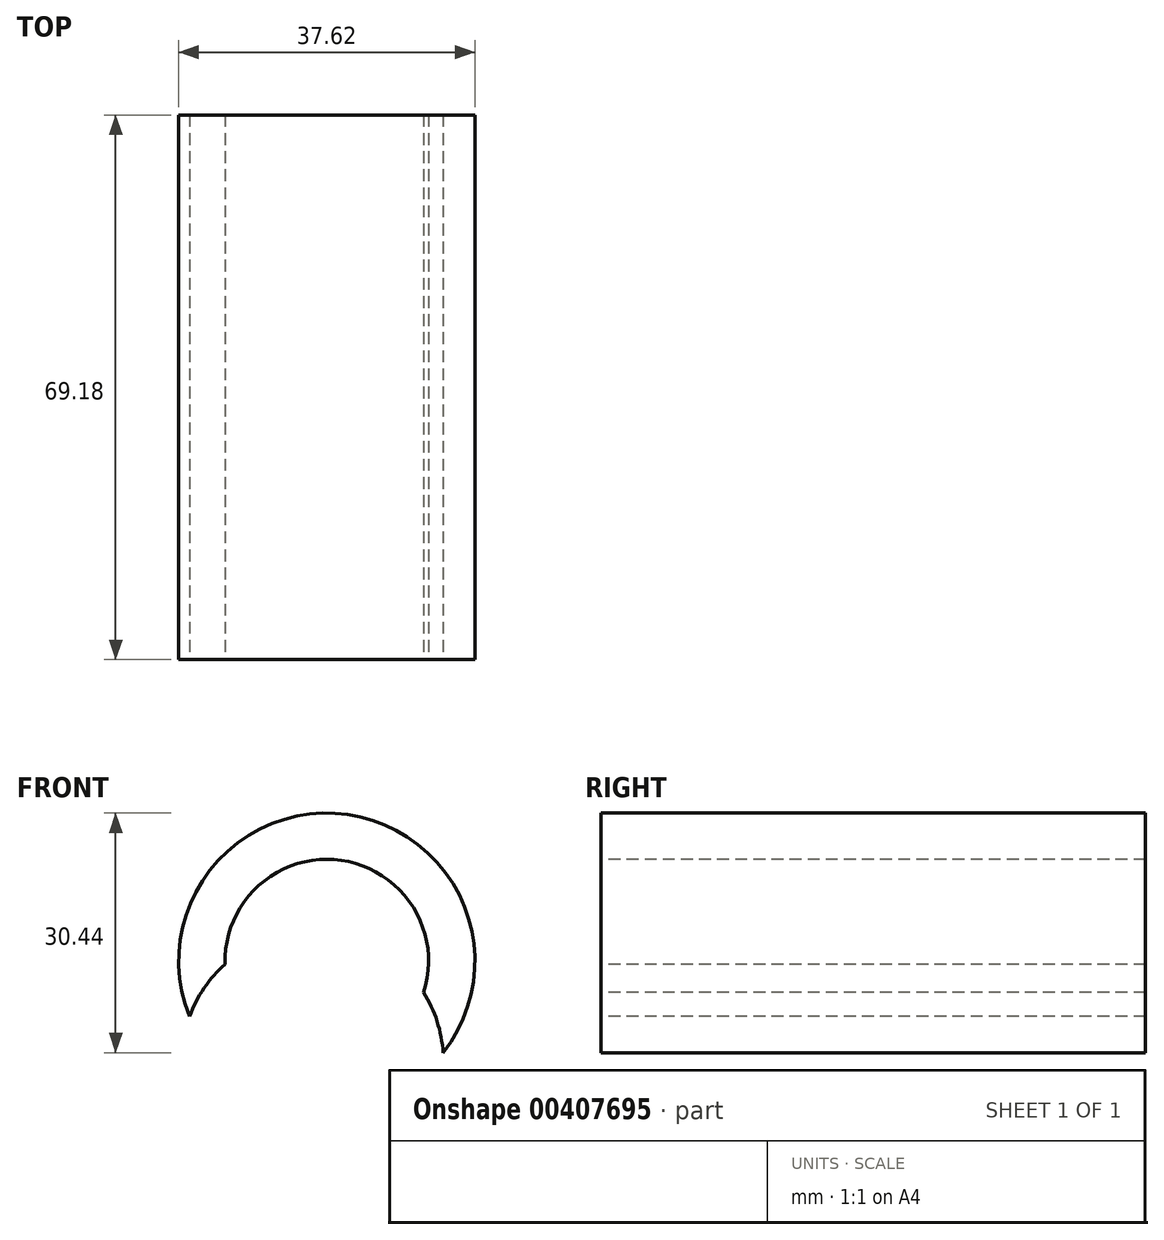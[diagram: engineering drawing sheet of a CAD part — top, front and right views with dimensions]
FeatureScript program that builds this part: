
annotation { "Feature Type Name" : "Feature", "Feature Type Description" : "" }
export const myFeature = defineFeature(function(context is Context, id is Id, definition is map)
    precondition{}
    {
        {
            var Q0;
            Q0=qCreatedBy(makeId("Front.planeOp"),FACE);
            var sketch = newSketch(context, id + "F0", { "sketchPlane" : qUnion([Q0])});
            skCircle(sketch, "E0", {"center": v(0, 77.76) * mm, "radius": 18.8 * mm});
            skSolve(sketch);
        }
        {
            var Q0;
            Q0 = qSketchRegion(id + "F0", true);
            extrude(context, id + "F1", {"entities" : qUnion([Q0]), "depth" : 69.18 * mm});
        }
        {
            var Q0;
            Q0=makeQuery(id+"F1.opExtrude","CAP_FACE",FACE,{"disambiguationData":[OSD([sQuery(id+"F0.wireOp",EDGE,"E0")])],"isStart":false});
            var sketch = newSketch(context, id + "F2", { "sketchPlane" : qUnion([Q0])});
            skCircle(sketch, "E1", {"center": v(0, 77.76) * mm, "radius": 12.93 * mm});
            skSolve(sketch);
        }
        {
            var Q0;
            Q0 = qSketchRegion(id + "F2", true);
            extrude(context, id + "F3", {"entities" : qUnion([Q0]), "operationType" : NewBodyOperationType.REMOVE, "oppositeDirection" : true, "depth" : 129.73 * mm});
        }
        {
            var Q0;
            Q0=makeQuery(id+"F1.opExtrude","CAP_FACE",FACE,{"disambiguationData":[OSD([sQuery(id+"F0.wireOp",EDGE,"E0")])],"isStart":false});
            var sketch = newSketch(context, id + "F4", { "sketchPlane" : qUnion([Q0])});
            skCircle(sketch, "E2", {"center": v(0, 64.83) * mm, "radius": 18.18 * mm});
            skSolve(sketch);
        }
        {
            var Q0;
            {var subQ0=sQuery(id+"F4.wireOp",EDGE,"E2");var subQ1=makeQuery(id+"F3.boolean.opBoolean","COPY",EDGE,{"derivedFrom":makeQuery(id+"F3.opExtrude","CAP_EDGE",EDGE,{"disambiguationData":[OSD([sQuery(id+"F2.wireOp",EDGE,"E1")])],"isStart":true})});var subQ2=makeQuery(id+"F4.imprint","INTERSECT",VERTEX,{"disambiguationData":[OD(0.0)],"derivedFrom":[subQ1,subQ0]});Q0=makeQuery(id+"F4.imprint","IMPRINT",FACE,{"disambiguationData":[TD([[makeQuery(id+"F4.imprint","IMPRINT",EDGE,{"disambiguationData":[TD([[subQ2,-1.0]])],"derivedFrom":subQ0}),1.0]])]});}
            var Q1;
            {var subQ0=sQuery(id+"F4.wireOp",EDGE,"E2");var subQ1=makeQuery(id+"F1.opExtrude","CAP_EDGE",EDGE,{"disambiguationData":[OSD([sQuery(id+"F0.wireOp",EDGE,"E0")])],"isStart":false});var subQ2=makeQuery(id+"F4.imprint","INTERSECT",VERTEX,{"disambiguationData":[OD(0.0)],"derivedFrom":[subQ1,subQ0]});Q1=makeQuery(id+"F4.imprint","IMPRINT",FACE,{"disambiguationData":[TD([[makeQuery(id+"F4.imprint","IMPRINT",EDGE,{"disambiguationData":[TD([[subQ2,1.0]])],"derivedFrom":subQ0}),1.0]])]});}
            extrude(context, id + "F5", {"entities" : qUnion([Q0, Q1]), "operationType" : NewBodyOperationType.REMOVE, "oppositeDirection" : true, "depth" : 129.6 * mm});
        }
        {
            var Q0;
            Q0=makeQuery(id+"F1.opExtrude","CAP_FACE",FACE,{"disambiguationData":[OSD([sQuery(id+"F0.wireOp",EDGE,"E0")])],"isStart":false});
            var sketch = newSketch(context, id + "F6", { "sketchPlane" : qUnion([Q0])});
            skCircle(sketch, "E3", {"center": v(-1.83, 64.96) * mm, "radius": 16.65 * mm});
            skSolve(sketch);
        }
        {
            var Q0;
            Q0 = qSketchRegion(id + "F6", true);
            extrude(context, id + "F7", {"entities" : qUnion([Q0]), "operationType" : NewBodyOperationType.REMOVE, "oppositeDirection" : true, "depth" : 87.64 * mm});
        }
    });
